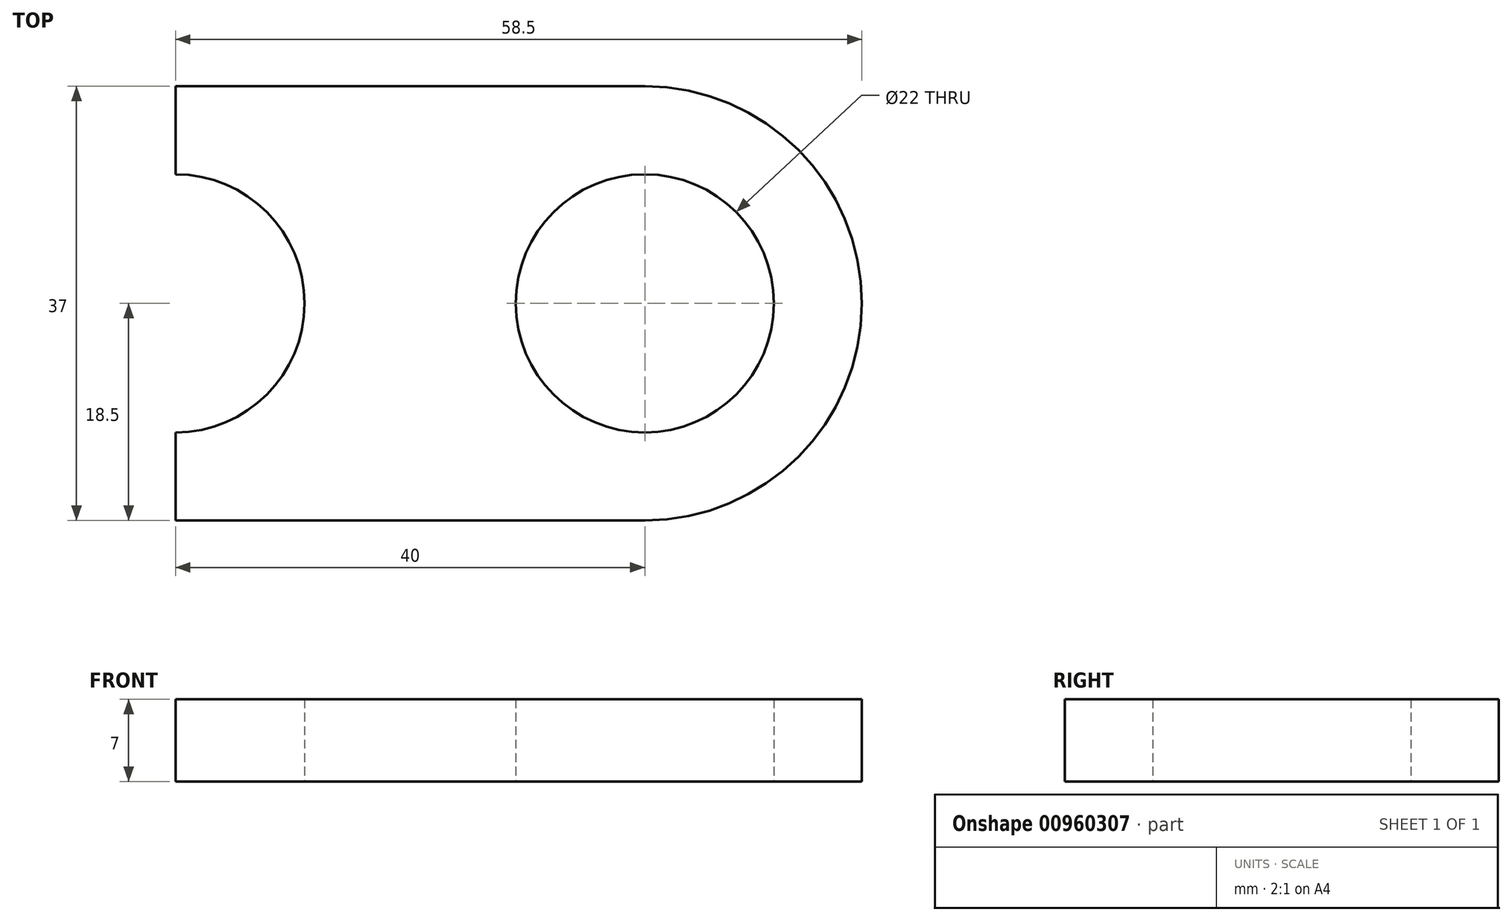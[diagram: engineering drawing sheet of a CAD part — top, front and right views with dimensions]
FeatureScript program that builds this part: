
annotation { "Feature Type Name" : "Feature", "Feature Type Description" : "" }
export const myFeature = defineFeature(function(context is Context, id is Id, definition is map)
    precondition{}
    {
        {
            var Q0;
            Q0=qCreatedBy(makeId("Top.planeOp"),FACE);
            var sketch = newSketch(context, id + "F0", { "sketchPlane" : qUnion([Q0])});
            skCircle(sketch, "E0", {"center": v(0, 0) * mm, "radius": 11 * mm});
            skLineSegment(sketch, "E1", {"start": v(0, 0) * mm, "end": v(40, 0) * mm, "construction": true});
            skCircle(sketch, "E2", {"center": v(40, 0) * mm, "radius": 11 * mm});
            skLineSegment(sketch, "E3", {"start": v(40, 0) * mm, "end": v(40, 18.5) * mm, "construction": true});
            skLineSegment(sketch, "E4", {"start": v(40, 0) * mm, "end": v(40, -18.5) * mm, "construction": true});
            skLineSegment(sketch, "E5", {"start": v(40, 0) * mm, "end": v(58.5, 0) * mm, "construction": true});
            skArc(sketch, "E6", {"start": v(40, -18.5) * mm, "mid": v(58.5, 0) * mm, "end": v(40, 18.5) * mm});
            skLineSegment(sketch, "E7", {"start": v(40, 18.5) * mm, "end": v(0, 18.5) * mm});
            skLineSegment(sketch, "E8", {"start": v(40, -18.5) * mm, "end": v(0, -18.5) * mm});
            skLineSegment(sketch, "E9", {"start": v(0, 18.5) * mm, "end": v(0, 11) * mm});
            skLineSegment(sketch, "E10", {"start": v(0, -18.5) * mm, "end": v(0, -11) * mm});
            skSolve(sketch);
        }
        {
            var Q0;
            Q0=makeQuery(id+"F0.imprint","IMPRINT",FACE,{"disambiguationData":[TD([[makeQuery(id+"F0.imprint","IMPRINT",EDGE,{"derivedFrom":sQuery(id+"F0.wireOp",EDGE,"E2")}),-1.0]])]});
            extrude(context, id + "F1", {"entities" : qUnion([Q0]), "depth" : 7 * mm, "offsetDistance" : 25 * mm});
        }
    });
